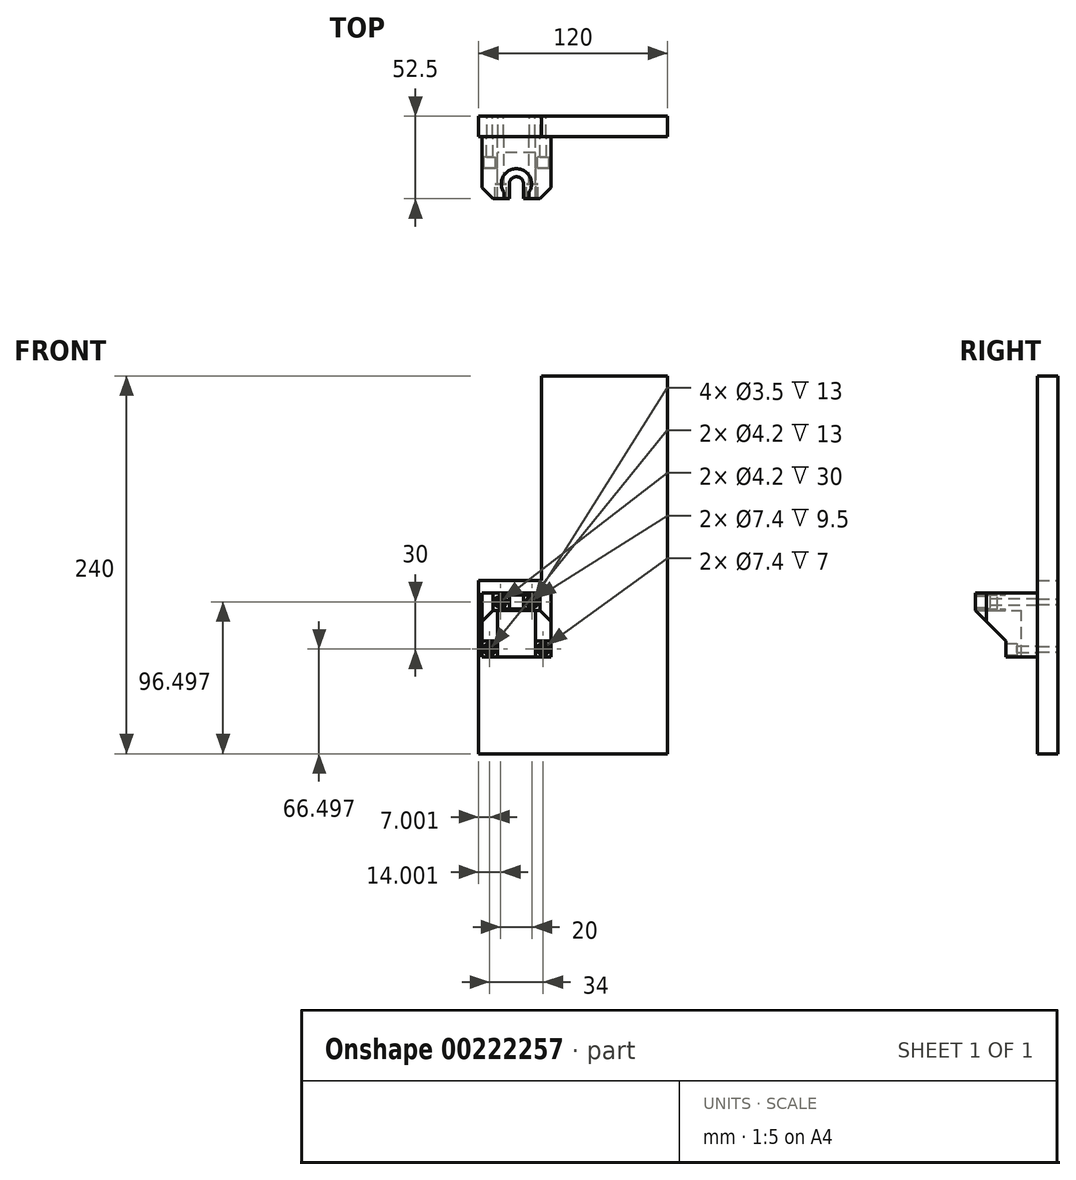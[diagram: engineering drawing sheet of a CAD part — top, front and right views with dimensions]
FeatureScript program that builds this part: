
annotation { "Feature Type Name" : "Feature", "Feature Type Description" : "" }
export const myFeature = defineFeature(function(context is Context, id is Id, definition is map)
    precondition{}
    {
        {
            var Q0;
            Q0=qCreatedBy(makeId("Front.planeOp"),FACE);
            var sketch = newSketch(context, id + "F0", { "sketchPlane" : qUnion([Q0])});
            skLineSegment(sketch, "E0", {"start": v(-58.67, 54.39) * mm, "end": v(-18.67, 54.39) * mm});
            skLineSegment(sketch, "E1", {"start": v(-18.67, 54.39) * mm, "end": v(-18.67, 184.39) * mm});
            skLineSegment(sketch, "E2", {"start": v(-18.67, 184.39) * mm, "end": v(61.33, 184.39) * mm});
            skLineSegment(sketch, "E3", {"start": v(61.33, 184.39) * mm, "end": v(61.33, -55.61) * mm});
            skLineSegment(sketch, "E4", {"start": v(61.33, -55.61) * mm, "end": v(-58.67, -55.61) * mm});
            skLineSegment(sketch, "E5", {"start": v(-58.67, -55.61) * mm, "end": v(-58.67, 54.39) * mm});
            skPoint(sketch, "E6", {"position": v(-44.67, 40.89) * mm});
            skPoint(sketch, "E7", {"position": v(-24.67, 40.89) * mm});
            skPoint(sketch, "E8", {"position": v(-51.67, 10.89) * mm});
            skPoint(sketch, "E9", {"position": v(-17.67, 10.89) * mm});
            skSolve(sketch);
        }
        {
            var Q0;
            Q0=makeQuery(id+"F0.imprint","IMPRINT",FACE,{"disambiguationData":[TD([[makeQuery(id+"F0.imprint","IMPRINT",EDGE,{"derivedFrom":sQuery(id+"F0.wireOp",EDGE,"E0")}),-1.0]])]});
            extrude(context, id + "F1", {"entities" : qUnion([Q0]), "depth" : 13 * mm});
        }
        {
            var Q0;
            Q0=sQuery(id+"F0.wireOp",VERTEX,"E6");
            var Q1;
            Q1=sQuery(id+"F0.wireOp",VERTEX,"E7");
            var Q2;
            Q2=sQuery(id+"F0.wireOp",VERTEX,"E8");
            var Q3;
            Q3=sQuery(id+"F0.wireOp",VERTEX,"E9");
            var Q4;
            Q4=makeQuery(id+"F1.opExtrude","SWEPT_BODY",BODY,{"disambiguationData":[OSD([sQuery(id+"F0.wireOp",EDGE,"E0"),sQuery(id+"F0.wireOp",EDGE,"E1"),sQuery(id+"F0.wireOp",EDGE,"E2"),sQuery(id+"F0.wireOp",EDGE,"E3"),sQuery(id+"F0.wireOp",EDGE,"E4"),sQuery(id+"F0.wireOp",EDGE,"E5")])]});
            hole(context, id + "F2", {"style" : HoleStyle.SIMPLE, "endStyle" : HoleEndStyle.THROUGH, "oppositeDirection" : true, "standardTappedOrClearance" : lookupTablePath({ "standard" : "ISO", "engagement" : "25%", "pitch" : "0.75 mm", "size" : "M4", "type" : "Tapped" }), "standardBlindInLast" : lookupTablePath({ "standard" : "ISO", "engagement" : "25%", "pitch" : "0.75 mm", "size" : "M4", "type" : "Tapped" }), "holeDiameter" : 3.5 * mm, "locations" : qUnion([Q0, Q1, Q2, Q3]), "scope" : qUnion([Q4]), "isTappedThrough" : true, "showTappedDepth" : true});
        }
        {
            var Q0;
            Q0=makeQuery(id+"F1.opExtrude","CAP_FACE",FACE,{"disambiguationData":[OSD([sQuery(id+"F0.wireOp",EDGE,"E0"),sQuery(id+"F0.wireOp",EDGE,"E1"),sQuery(id+"F0.wireOp",EDGE,"E2"),sQuery(id+"F0.wireOp",EDGE,"E3"),sQuery(id+"F0.wireOp",EDGE,"E4"),sQuery(id+"F0.wireOp",EDGE,"E5")])],"isStart":false});
            var sketch = newSketch(context, id + "F3", { "sketchPlane" : qUnion([Q0])});
            skLineSegment(sketch, "E10", {"start": v(-44.67, 40.89) * mm, "end": v(-24.67, 40.89) * mm, "construction": true});
            skLineSegment(sketch, "E11", {"start": v(-51.67, 10.89) * mm, "end": v(-17.67, 10.89) * mm, "construction": true});
            skLineSegment(sketch, "E12", {"start": v(-34.67, 40.89) * mm, "end": v(-34.67, 10.89) * mm, "construction": true});
            skLineSegment(sketch, "E13.bottom", {"start": v(-12.67, 5.89) * mm, "end": v(-56.67, 5.89) * mm});
            skLineSegment(sketch, "E13.top", {"start": v(-12.67, 46.39) * mm, "end": v(-56.67, 46.39) * mm});
            skLineSegment(sketch, "E13.left", {"start": v(-12.67, 5.89) * mm, "end": v(-12.67, 46.39) * mm});
            skLineSegment(sketch, "E13.right", {"start": v(-56.67, 5.89) * mm, "end": v(-56.67, 46.39) * mm});
            skCircle(sketch, "E14", {"center": v(-44.67, 40.89) * mm, "radius": 3.7 * mm});
            skCircle(sketch, "E15", {"center": v(-24.67, 40.89) * mm, "radius": 3.7 * mm});
            skCircle(sketch, "E16", {"center": v(-51.67, 10.89) * mm, "radius": 3.7 * mm});
            skCircle(sketch, "E17", {"center": v(-17.67, 10.89) * mm, "radius": 3.7 * mm});
            skCircle(sketch, "E18", {"center": v(-17.67, 10.89) * mm, "radius": 2.1 * mm});
            skCircle(sketch, "E19", {"center": v(-51.67, 10.89) * mm, "radius": 2.1 * mm});
            skCircle(sketch, "E20", {"center": v(-44.67, 40.89) * mm, "radius": 2.1 * mm});
            skCircle(sketch, "E21", {"center": v(-24.67, 40.89) * mm, "radius": 2.1 * mm});
            skLineSegment(sketch, "E22", {"start": v(-46.67, 5.89) * mm, "end": v(-46.67, 35.39) * mm});
            skLineSegment(sketch, "E23", {"start": v(-46.67, 35.39) * mm, "end": v(-22.67, 35.39) * mm});
            skLineSegment(sketch, "E24", {"start": v(-22.67, 35.39) * mm, "end": v(-22.67, 5.89) * mm});
            skSolve(sketch);
        }
        {
            var Q0;
            Q0=makeQuery(id+"F3.imprint","IMPRINT",FACE,{"disambiguationData":[TD([[makeQuery(id+"F3.imprint","IMPRINT",EDGE,{"derivedFrom":sQuery(id+"F3.wireOp",EDGE,"E13.bottom")}),-1.0]])]});
            var Q1;
            Q1=makeQuery(id+"F3.imprint","IMPRINT",FACE,{"disambiguationData":[TD([[makeQuery(id+"F3.imprint","IMPRINT",EDGE,{"derivedFrom":makeQuery(id+"F2.hole-0.boolean.opBoolean","INTERSECT",EDGE,{"derivedFrom":[makeQuery(id+"F1.opExtrude","CAP_FACE",FACE,{"disambiguationData":[OSD([sQuery(id+"F0.wireOp",EDGE,"E0"),sQuery(id+"F0.wireOp",EDGE,"E1"),sQuery(id+"F0.wireOp",EDGE,"E2"),sQuery(id+"F0.wireOp",EDGE,"E3"),sQuery(id+"F0.wireOp",EDGE,"E4"),sQuery(id+"F0.wireOp",EDGE,"E5")])],"isStart":false}),makeQuery(id+"F2.hole-0.opRevolve","SWEPT_FACE",FACE,{"disambiguationData":[OSD([sQuery(id+"F2.hole-0.sketch.wireOp",EDGE,"core_line_2")])]})]})}),-1.0]])]});
            var Q2;
            Q2=makeQuery(id+"F3.imprint","IMPRINT",FACE,{"disambiguationData":[TD([[makeQuery(id+"F3.imprint","IMPRINT",EDGE,{"derivedFrom":makeQuery(id+"F2.hole-1.boolean.opBoolean","INTERSECT",EDGE,{"derivedFrom":[makeQuery(id+"F1.opExtrude","CAP_FACE",FACE,{"disambiguationData":[OSD([sQuery(id+"F0.wireOp",EDGE,"E0"),sQuery(id+"F0.wireOp",EDGE,"E1"),sQuery(id+"F0.wireOp",EDGE,"E2"),sQuery(id+"F0.wireOp",EDGE,"E3"),sQuery(id+"F0.wireOp",EDGE,"E4"),sQuery(id+"F0.wireOp",EDGE,"E5")])],"isStart":false}),makeQuery(id+"F2.hole-1.opRevolve","SWEPT_FACE",FACE,{"disambiguationData":[OSD([sQuery(id+"F2.hole-1.sketch.wireOp",EDGE,"core_line_2")])]})]})}),-1.0]])]});
            var Q3;
            Q3=makeQuery(id+"F3.imprint","IMPRINT",FACE,{"disambiguationData":[TD([[makeQuery(id+"F3.imprint","IMPRINT",EDGE,{"derivedFrom":makeQuery(id+"F2.hole-3.boolean.opBoolean","INTERSECT",EDGE,{"derivedFrom":[makeQuery(id+"F1.opExtrude","CAP_FACE",FACE,{"disambiguationData":[OSD([sQuery(id+"F0.wireOp",EDGE,"E0"),sQuery(id+"F0.wireOp",EDGE,"E1"),sQuery(id+"F0.wireOp",EDGE,"E2"),sQuery(id+"F0.wireOp",EDGE,"E3"),sQuery(id+"F0.wireOp",EDGE,"E4"),sQuery(id+"F0.wireOp",EDGE,"E5")])],"isStart":false}),makeQuery(id+"F2.hole-3.opRevolve","SWEPT_FACE",FACE,{"disambiguationData":[OSD([sQuery(id+"F2.hole-3.sketch.wireOp",EDGE,"core_line_2")])]})]})}),-1.0]])]});
            var Q4;
            Q4=makeQuery(id+"F3.imprint","IMPRINT",FACE,{"disambiguationData":[TD([[makeQuery(id+"F3.imprint","IMPRINT",EDGE,{"derivedFrom":makeQuery(id+"F2.hole-2.boolean.opBoolean","INTERSECT",EDGE,{"derivedFrom":[makeQuery(id+"F1.opExtrude","CAP_FACE",FACE,{"disambiguationData":[OSD([sQuery(id+"F0.wireOp",EDGE,"E0"),sQuery(id+"F0.wireOp",EDGE,"E1"),sQuery(id+"F0.wireOp",EDGE,"E2"),sQuery(id+"F0.wireOp",EDGE,"E3"),sQuery(id+"F0.wireOp",EDGE,"E4"),sQuery(id+"F0.wireOp",EDGE,"E5")])],"isStart":false}),makeQuery(id+"F2.hole-2.opRevolve","SWEPT_FACE",FACE,{"disambiguationData":[OSD([sQuery(id+"F2.hole-2.sketch.wireOp",EDGE,"core_line_2")])]})]})}),-1.0]])]});
            var Q5;
            Q5=makeQuery(id+"F3.imprint","IMPRINT",FACE,{"disambiguationData":[TD([[makeQuery(id+"F3.imprint","IMPRINT",EDGE,{"derivedFrom":sQuery(id+"F3.wireOp",EDGE,"E16")}),1.0]])]});
            var Q6;
            Q6=makeQuery(id+"F3.imprint","IMPRINT",FACE,{"disambiguationData":[TD([[makeQuery(id+"F3.imprint","IMPRINT",EDGE,{"derivedFrom":sQuery(id+"F3.wireOp",EDGE,"E19")}),1.0]])]});
            var Q7;
            Q7=makeQuery(id+"F3.imprint","IMPRINT",FACE,{"disambiguationData":[TD([[makeQuery(id+"F3.imprint","IMPRINT",EDGE,{"derivedFrom":sQuery(id+"F3.wireOp",EDGE,"E17")}),1.0]])]});
            var Q8;
            Q8=makeQuery(id+"F3.imprint","IMPRINT",FACE,{"disambiguationData":[TD([[makeQuery(id+"F3.imprint","IMPRINT",EDGE,{"derivedFrom":sQuery(id+"F3.wireOp",EDGE,"E18")}),1.0]])]});
            var Q9;
            Q9=makeQuery(id+"F3.imprint","IMPRINT",FACE,{"disambiguationData":[TD([[makeQuery(id+"F3.imprint","IMPRINT",EDGE,{"derivedFrom":sQuery(id+"F3.wireOp",EDGE,"E15")}),1.0]])]});
            var Q10;
            Q10=makeQuery(id+"F3.imprint","IMPRINT",FACE,{"disambiguationData":[TD([[makeQuery(id+"F3.imprint","IMPRINT",EDGE,{"derivedFrom":sQuery(id+"F3.wireOp",EDGE,"E21")}),1.0]])]});
            var Q11;
            Q11=makeQuery(id+"F3.imprint","IMPRINT",FACE,{"disambiguationData":[TD([[makeQuery(id+"F3.imprint","IMPRINT",EDGE,{"derivedFrom":sQuery(id+"F3.wireOp",EDGE,"E20")}),1.0]])]});
            var Q12;
            Q12=makeQuery(id+"F3.imprint","IMPRINT",FACE,{"disambiguationData":[TD([[makeQuery(id+"F3.imprint","IMPRINT",EDGE,{"derivedFrom":sQuery(id+"F3.wireOp",EDGE,"E14")}),1.0]])]});
            extrude(context, id + "F4", {"entities" : qUnion([Q0, Q1, Q2, Q3, Q4, Q5, Q6, Q7, Q8, Q9, Q10, Q11, Q12]), "depth" : 39.5 * mm});
        }
        {
            var Q0;
            Q0=makeQuery(id+"F3.imprint","IMPRINT",FACE,{"disambiguationData":[TD([[makeQuery(id+"F3.imprint","IMPRINT",EDGE,{"derivedFrom":makeQuery(id+"F2.hole-1.boolean.opBoolean","INTERSECT",EDGE,{"derivedFrom":[makeQuery(id+"F1.opExtrude","CAP_FACE",FACE,{"disambiguationData":[OSD([sQuery(id+"F0.wireOp",EDGE,"E0"),sQuery(id+"F0.wireOp",EDGE,"E1"),sQuery(id+"F0.wireOp",EDGE,"E2"),sQuery(id+"F0.wireOp",EDGE,"E3"),sQuery(id+"F0.wireOp",EDGE,"E4"),sQuery(id+"F0.wireOp",EDGE,"E5")])],"isStart":false}),makeQuery(id+"F2.hole-1.opRevolve","SWEPT_FACE",FACE,{"disambiguationData":[OSD([sQuery(id+"F2.hole-1.sketch.wireOp",EDGE,"core_line_2")])]})]})}),-1.0]])]});
            var Q1;
            Q1=makeQuery(id+"F3.imprint","IMPRINT",FACE,{"disambiguationData":[TD([[makeQuery(id+"F3.imprint","IMPRINT",EDGE,{"derivedFrom":sQuery(id+"F3.wireOp",EDGE,"E21")}),1.0]])]});
            var Q2;
            Q2=makeQuery(id+"F3.imprint","IMPRINT",FACE,{"disambiguationData":[TD([[makeQuery(id+"F3.imprint","IMPRINT",EDGE,{"derivedFrom":sQuery(id+"F3.wireOp",EDGE,"E20")}),1.0]])]});
            var Q3;
            Q3=makeQuery(id+"F3.imprint","IMPRINT",FACE,{"disambiguationData":[TD([[makeQuery(id+"F3.imprint","IMPRINT",EDGE,{"derivedFrom":makeQuery(id+"F2.hole-0.boolean.opBoolean","INTERSECT",EDGE,{"derivedFrom":[makeQuery(id+"F1.opExtrude","CAP_FACE",FACE,{"disambiguationData":[OSD([sQuery(id+"F0.wireOp",EDGE,"E0"),sQuery(id+"F0.wireOp",EDGE,"E1"),sQuery(id+"F0.wireOp",EDGE,"E2"),sQuery(id+"F0.wireOp",EDGE,"E3"),sQuery(id+"F0.wireOp",EDGE,"E4"),sQuery(id+"F0.wireOp",EDGE,"E5")])],"isStart":false}),makeQuery(id+"F2.hole-0.opRevolve","SWEPT_FACE",FACE,{"disambiguationData":[OSD([sQuery(id+"F2.hole-0.sketch.wireOp",EDGE,"core_line_2")])]})]})}),-1.0]])]});
            var Q4;
            Q4=makeQuery(id+"F3.imprint","IMPRINT",FACE,{"disambiguationData":[TD([[makeQuery(id+"F3.imprint","IMPRINT",EDGE,{"derivedFrom":makeQuery(id+"F2.hole-3.boolean.opBoolean","INTERSECT",EDGE,{"derivedFrom":[makeQuery(id+"F1.opExtrude","CAP_FACE",FACE,{"disambiguationData":[OSD([sQuery(id+"F0.wireOp",EDGE,"E0"),sQuery(id+"F0.wireOp",EDGE,"E1"),sQuery(id+"F0.wireOp",EDGE,"E2"),sQuery(id+"F0.wireOp",EDGE,"E3"),sQuery(id+"F0.wireOp",EDGE,"E4"),sQuery(id+"F0.wireOp",EDGE,"E5")])],"isStart":false}),makeQuery(id+"F2.hole-3.opRevolve","SWEPT_FACE",FACE,{"disambiguationData":[OSD([sQuery(id+"F2.hole-3.sketch.wireOp",EDGE,"core_line_2")])]})]})}),-1.0]])]});
            var Q5;
            Q5=makeQuery(id+"F3.imprint","IMPRINT",FACE,{"disambiguationData":[TD([[makeQuery(id+"F3.imprint","IMPRINT",EDGE,{"derivedFrom":sQuery(id+"F3.wireOp",EDGE,"E18")}),1.0]])]});
            var Q6;
            Q6=makeQuery(id+"F3.imprint","IMPRINT",FACE,{"disambiguationData":[TD([[makeQuery(id+"F3.imprint","IMPRINT",EDGE,{"derivedFrom":makeQuery(id+"F2.hole-2.boolean.opBoolean","INTERSECT",EDGE,{"derivedFrom":[makeQuery(id+"F1.opExtrude","CAP_FACE",FACE,{"disambiguationData":[OSD([sQuery(id+"F0.wireOp",EDGE,"E0"),sQuery(id+"F0.wireOp",EDGE,"E1"),sQuery(id+"F0.wireOp",EDGE,"E2"),sQuery(id+"F0.wireOp",EDGE,"E3"),sQuery(id+"F0.wireOp",EDGE,"E4"),sQuery(id+"F0.wireOp",EDGE,"E5")])],"isStart":false}),makeQuery(id+"F2.hole-2.opRevolve","SWEPT_FACE",FACE,{"disambiguationData":[OSD([sQuery(id+"F2.hole-2.sketch.wireOp",EDGE,"core_line_2")])]})]})}),-1.0]])]});
            var Q7;
            Q7=makeQuery(id+"F3.imprint","IMPRINT",FACE,{"disambiguationData":[TD([[makeQuery(id+"F3.imprint","IMPRINT",EDGE,{"derivedFrom":sQuery(id+"F3.wireOp",EDGE,"E19")}),1.0]])]});
            extrude(context, id + "F5", {"entities" : qUnion([Q0, Q1, Q2, Q3, Q4, Q5, Q6, Q7]), "operationType" : NewBodyOperationType.REMOVE, "endBound" : BoundingType.THROUGH_ALL, "depth" : 25 * mm});
        }
        {
            var Q0;
            Q0=makeQuery(id+"F3.imprint","IMPRINT",FACE,{"disambiguationData":[TD([[makeQuery(id+"F3.imprint","IMPRINT",EDGE,{"derivedFrom":sQuery(id+"F3.wireOp",EDGE,"E14")}),1.0]])]});
            var Q1;
            Q1=makeQuery(id+"F3.imprint","IMPRINT",FACE,{"disambiguationData":[TD([[makeQuery(id+"F3.imprint","IMPRINT",EDGE,{"derivedFrom":sQuery(id+"F3.wireOp",EDGE,"E15")}),1.0]])]});
            extrude(context, id + "F6", {"entities" : qUnion([Q0, Q1]), "operationType" : NewBodyOperationType.REMOVE, "endBound" : BoundingType.THROUGH_ALL, "depth" : 40.2 * mm, "hasSecondDirection" : true, "secondDirectionOppositeDirection" : false, "secondDirectionDepth" : 30 * mm});
        }
        {
            var Q0;
            Q0=makeQuery(id+"F3.imprint","IMPRINT",FACE,{"disambiguationData":[TD([[makeQuery(id+"F3.imprint","IMPRINT",EDGE,{"derivedFrom":sQuery(id+"F3.wireOp",EDGE,"E17")}),1.0]])]});
            var Q1;
            Q1=makeQuery(id+"F3.imprint","IMPRINT",FACE,{"disambiguationData":[TD([[makeQuery(id+"F3.imprint","IMPRINT",EDGE,{"derivedFrom":sQuery(id+"F3.wireOp",EDGE,"E16")}),1.0]])]});
            extrude(context, id + "F7", {"entities" : qUnion([Q0, Q1]), "operationType" : NewBodyOperationType.REMOVE, "endBound" : BoundingType.THROUGH_ALL, "depth" : 25 * mm, "hasSecondDirection" : true, "secondDirectionOppositeDirection" : false, "secondDirectionDepth" : 13 * mm});
        }
        {
            var Q0;
            Q0=makeQuery(id+"F4.opExtrude","SWEPT_FACE",FACE,{"disambiguationData":[OSD([sQuery(id+"F3.wireOp",EDGE,"E13.top")])]});
            var sketch = newSketch(context, id + "F8", { "sketchPlane" : qUnion([Q0])});
            skArc(sketch, "E25", {"start": v(-26.67, -48.3) * mm, "mid": v(-34.67, -33.4) * mm, "end": v(-42.67, -48.3) * mm});
            skPoint(sketch, "E25.centerSnap0", {"position": v(-34.67, -13) * mm});
            skArc(sketch, "E26", {"start": v(-30.17, -43) * mm, "mid": v(-34.67, -38.5) * mm, "end": v(-39.17, -43) * mm});
            skLineSegment(sketch, "E27", {"start": v(-42.67, -48.3) * mm, "end": v(-42.67, -52.5) * mm});
            skLineSegment(sketch, "E28", {"start": v(-26.67, -48.3) * mm, "end": v(-26.67, -52.5) * mm});
            skLineSegment(sketch, "E29", {"start": v(-39.17, -43) * mm, "end": v(-39.17, -52.5) * mm});
            skLineSegment(sketch, "E30", {"start": v(-30.17, -43) * mm, "end": v(-30.17, -52.5) * mm});
            skSolve(sketch);
        }
        {
            var Q0;
            {var subQ0=sQuery(id+"F3.wireOp",EDGE,"E22");Q0=makeQuery(id+"F3.imprint","IMPRINT",FACE,{"disambiguationData":[TD([[makeQuery(id+"F3.imprint","IMPRINT",EDGE,{"derivedFrom":subQ0}),-1.0]])]});}
            extrude(context, id + "F9", {"entities" : qUnion([Q0]), "operationType" : NewBodyOperationType.ADD, "depth" : 10 * mm});
        }
        {
            var Q0;
            Q0=makeQuery(id+"F4.opExtrude","SWEPT_FACE",FACE,{"disambiguationData":[OSD([sQuery(id+"F3.wireOp",EDGE,"E13.right")])]});
            var sketch = newSketch(context, id + "F10", { "sketchPlane" : qUnion([Q0])});
            skLineSegment(sketch, "E31", {"start": v(52.5, 35.39) * mm, "end": v(33, 15.89) * mm});
            skLineSegment(sketch, "E32", {"start": v(33, 15.89) * mm, "end": v(33, 5.89) * mm});
            skSolve(sketch);
        }
        {
            var Q0;
            {var subQ0=sQuery(id+"F10.wireOp",EDGE,"E31");Q0=makeQuery(id+"F10.imprint","IMPRINT",FACE,{"disambiguationData":[TD([[makeQuery(id+"F10.imprint","IMPRINT",EDGE,{"derivedFrom":subQ0}),1.0]])]});}
            extrude(context, id + "F11", {"entities" : qUnion([Q0]), "operationType" : NewBodyOperationType.REMOVE, "endBound" : BoundingType.THROUGH_ALL, "oppositeDirection" : true, "depth" : 25 * mm});
        }
        {
            var Q0;
            Q0=makeQuery(id+"F8.imprint","IMPRINT",FACE,{"disambiguationData":[TD([[makeQuery(id+"F8.imprint","IMPRINT",EDGE,{"derivedFrom":sQuery(id+"F8.wireOp",EDGE,"E26")}),1.0]])]});
            extrude(context, id + "F12", {"entities" : qUnion([Q0]), "operationType" : NewBodyOperationType.REMOVE, "endBound" : BoundingType.THROUGH_ALL, "oppositeDirection" : true, "depth" : 25 * mm});
        }
        {
            var Q0;
            Q0=makeQuery(id+"F8.imprint","IMPRINT",FACE,{"disambiguationData":[TD([[makeQuery(id+"F8.imprint","IMPRINT",EDGE,{"derivedFrom":sQuery(id+"F8.wireOp",EDGE,"E25")}),1.0]])]});
            extrude(context, id + "F13", {"entities" : qUnion([Q0]), "operationType" : NewBodyOperationType.REMOVE, "oppositeDirection" : true, "depth" : 1 * mm});
        }
        {
            var Q0;
            Q0=makeQuery(id+"F8.imprint","IMPRINT",FACE,{"disambiguationData":[TD([[makeQuery(id+"F8.imprint","IMPRINT",EDGE,{"derivedFrom":sQuery(id+"F8.wireOp",EDGE,"E25")}),1.0]])]});
            extrude(context, id + "F14", {"entities" : qUnion([Q0]), "operationType" : NewBodyOperationType.REMOVE, "endBound" : BoundingType.THROUGH_ALL, "oppositeDirection" : true, "depth" : 11.4 * mm, "hasSecondDirection" : true, "secondDirectionOppositeDirection" : true, "secondDirectionDepth" : 10 * mm});
        }
        {
            var Q0;
            Q0=makeQuery(id+"F4.opExtrude","CAP_EDGE",EDGE,{"disambiguationData":[OSD([sQuery(id+"F3.wireOp",EDGE,"E13.right")])],"isStart":false});
            var Q1;
            Q1=makeQuery(id+"F4.opExtrude","CAP_EDGE",EDGE,{"disambiguationData":[OSD([sQuery(id+"F3.wireOp",EDGE,"E13.left")])],"isStart":false});
            chamfer(context, id + "F15", {"entities" : qUnion([Q0, Q1]), "width" : 7 * mm, "tangentPropagation" : true});
        }
    });
